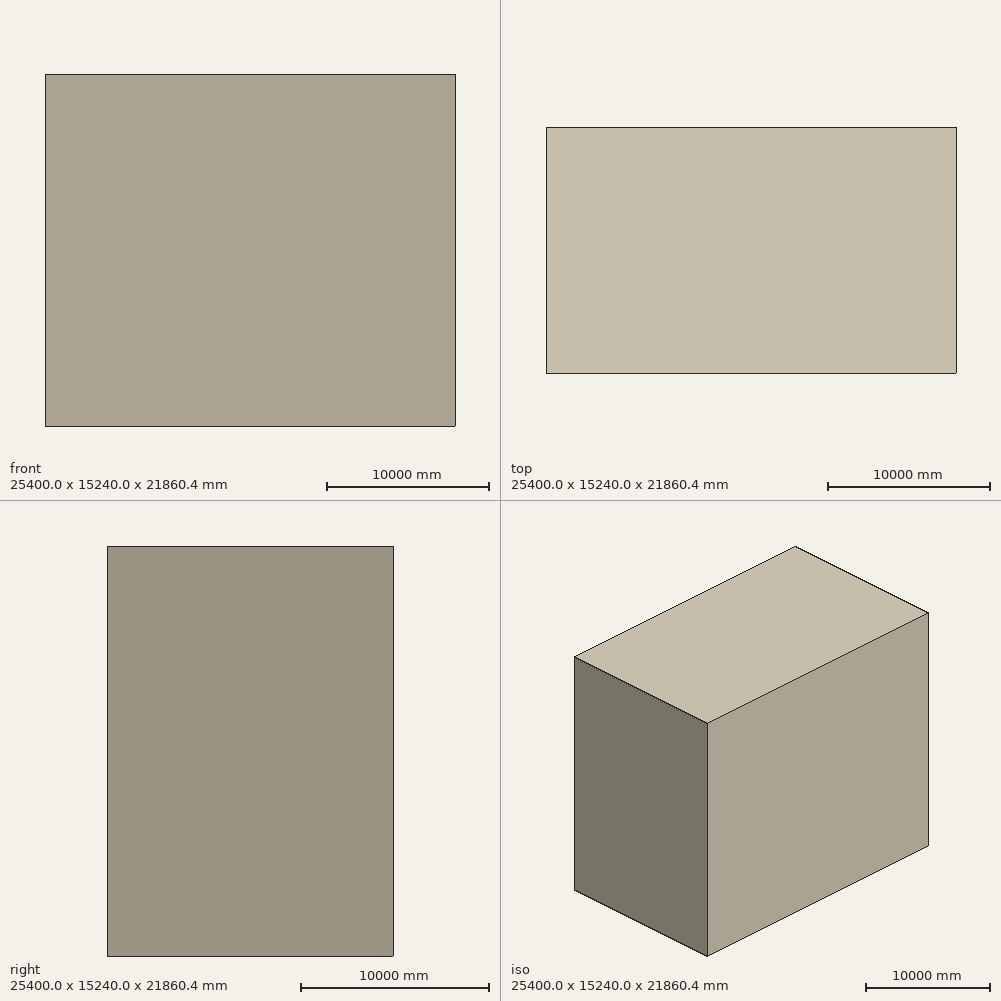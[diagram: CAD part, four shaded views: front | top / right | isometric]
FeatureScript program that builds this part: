
annotation { "Feature Type Name" : "Feature", "Feature Type Description" : "" }
export const myFeature = defineFeature(function(context is Context, id is Id, definition is map)
    precondition{}
    {
        {
            var Q0;
            Q0=qCreatedBy(makeId("Front.planeOp"),FACE);
            var sketch = newSketch(context, id + "F0", { "sketchPlane" : qUnion([Q0])});
            skLineSegment(sketch, "E0.bottom", {"start": v(12700, -10930.2) * mm, "end": v(-12700, -10930.2) * mm});
            skLineSegment(sketch, "E0.top", {"start": v(12700, 10930.2) * mm, "end": v(-12700, 10930.2) * mm});
            skLineSegment(sketch, "E0.left", {"start": v(12700, -10930.2) * mm, "end": v(12700, 10930.2) * mm});
            skLineSegment(sketch, "E0.right", {"start": v(-12700, -10930.2) * mm, "end": v(-12700, 10930.2) * mm});
            skPoint(sketch, "E0.middle", {"position": v(0, 0) * mm});
            skSolve(sketch);
        }
        {
            var Q0;
            Q0 = qSketchRegion(id + "F0", true);
            extrude(context, id + "F1", {"entities" : qUnion([Q0]), "depth" : 15240 * mm, "offsetDistance" : 25.4 * mm});
        }
    });
